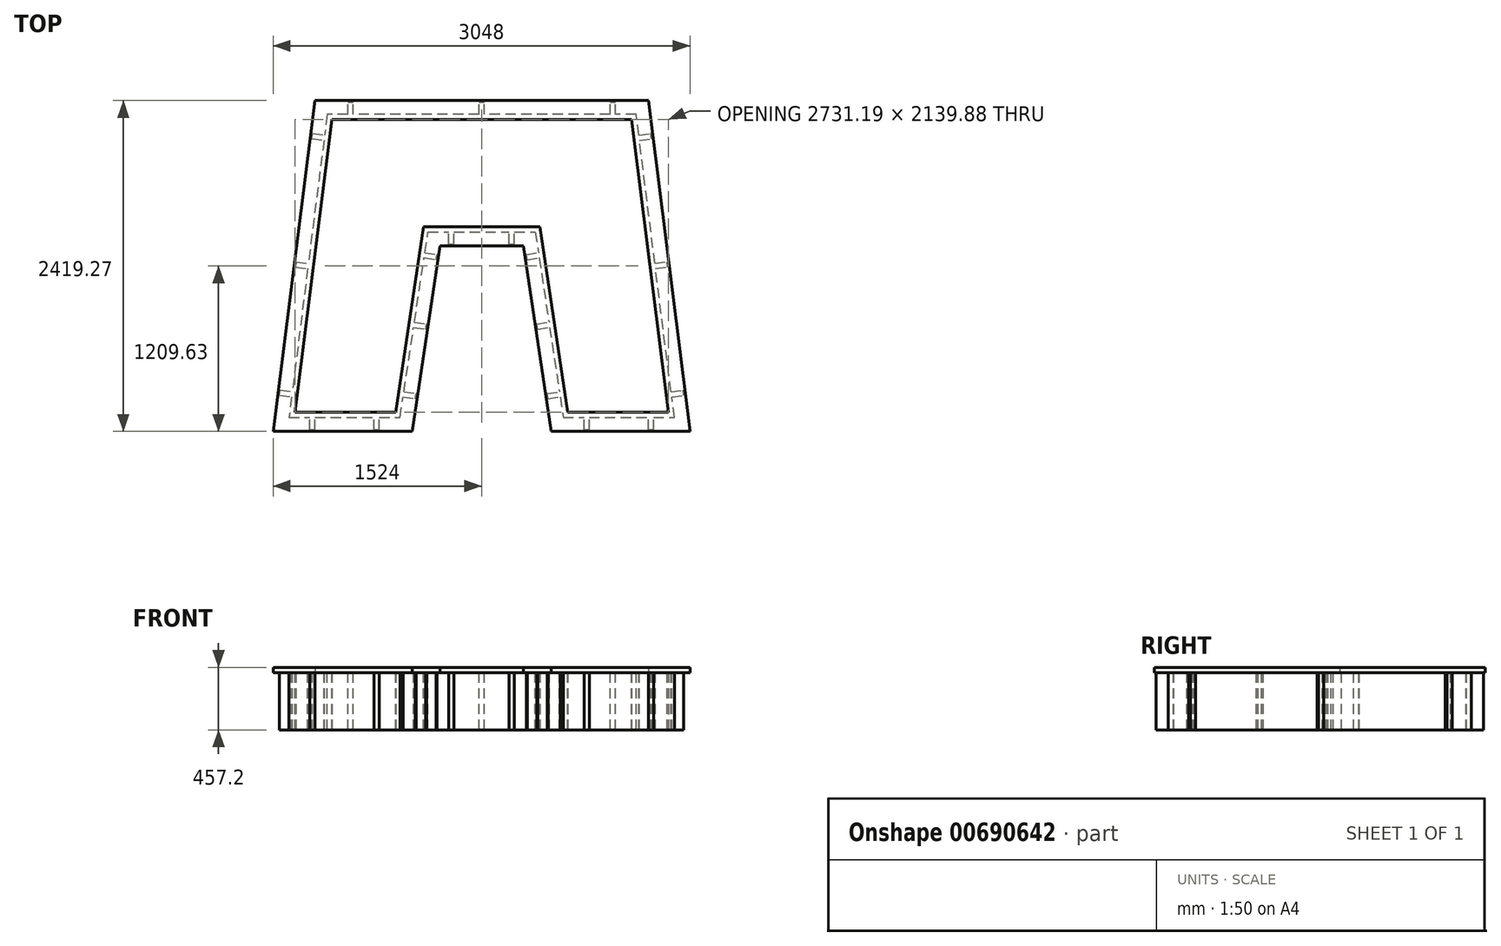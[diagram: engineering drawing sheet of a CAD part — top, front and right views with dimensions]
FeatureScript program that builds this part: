
annotation { "Feature Type Name" : "Feature", "Feature Type Description" : "" }
export const myFeature = defineFeature(function(context is Context, id is Id, definition is map)
    precondition{}
    {
        {
            var Q0;
            Q0=qCreatedBy(makeId("Top.planeOp"),FACE);
            var sketch = newSketch(context, id + "F0", { "sketchPlane" : qUnion([Q0])});
            skLineSegment(sketch, "E0", {"start": v(-1219.2, 0) * mm, "end": v(1219.2, 0) * mm});
            skLineSegment(sketch, "E1", {"start": v(1219.2, 0) * mm, "end": v(1524, -2419.27) * mm});
            skLineSegment(sketch, "E2", {"start": v(1524, -2419.27) * mm, "end": v(509.02, -2419.27) * mm});
            skLineSegment(sketch, "E3", {"start": v(509.02, -2419.27) * mm, "end": v(304.8, -1062.96) * mm});
            skLineSegment(sketch, "E4", {"start": v(304.8, -1062.96) * mm, "end": v(-304.8, -1062.96) * mm});
            skLineSegment(sketch, "E5", {"start": v(-304.8, -1062.96) * mm, "end": v(-509.02, -2419.27) * mm});
            skLineSegment(sketch, "E6", {"start": v(-509.02, -2419.27) * mm, "end": v(-1524, -2419.27) * mm});
            skLineSegment(sketch, "E7", {"start": v(-1524, -2419.27) * mm, "end": v(-1219.2, 0) * mm});
            skLineSegment(sketch, "E8", {"start": v(0, 98.61) * mm, "end": v(0, -258.13) * mm, "construction": true});
            skSolve(sketch);
        }
        {
            var Q0;
            Q0 = qSketchRegion(id + "F0", true);
            extrude(context, id + "F1", {"entities" : qUnion([Q0]), "depth" : 38.1 * mm, "offsetDistance" : 25.4 * mm});
        }
        {
            var Q0;
            Q0=makeQuery(id+"F1.opExtrude","CAP_FACE",FACE,{"disambiguationData":[OSD([sQuery(id+"F0.wireOp",EDGE,"E0"),sQuery(id+"F0.wireOp",EDGE,"E1"),sQuery(id+"F0.wireOp",EDGE,"E2"),sQuery(id+"F0.wireOp",EDGE,"E3"),sQuery(id+"F0.wireOp",EDGE,"E4"),sQuery(id+"F0.wireOp",EDGE,"E5"),sQuery(id+"F0.wireOp",EDGE,"E6"),sQuery(id+"F0.wireOp",EDGE,"E7")])],"isStart":false});
            var sketch = newSketch(context, id + "F2", { "sketchPlane" : qUnion([Q0])});
            skLineSegment(sketch, "E9", {"start": v(-1096, -139.7) * mm, "end": v(-1365.6, -2279.57) * mm});
            skLineSegment(sketch, "E10", {"start": v(-1365.6, -2279.57) * mm, "end": v(-629.26, -2279.57) * mm});
            skLineSegment(sketch, "E11", {"start": v(-629.26, -2279.57) * mm, "end": v(-425.04, -923.26) * mm});
            skLineSegment(sketch, "E12", {"start": v(-425.04, -923.26) * mm, "end": v(425.04, -923.26) * mm});
            skLineSegment(sketch, "E13", {"start": v(425.04, -923.26) * mm, "end": v(629.26, -2279.57) * mm});
            skLineSegment(sketch, "E14", {"start": v(629.26, -2279.57) * mm, "end": v(1365.6, -2279.57) * mm});
            skLineSegment(sketch, "E15", {"start": v(1365.6, -2279.57) * mm, "end": v(1096, -139.7) * mm});
            skLineSegment(sketch, "E16", {"start": v(1096, -139.7) * mm, "end": v(-1096, -139.7) * mm});
            skSolve(sketch);
        }
        {
            var Q0;
            Q0 = qSketchRegion(id + "F2", true);
            extrude(context, id + "F3", {"entities" : qUnion([Q0]), "operationType" : NewBodyOperationType.REMOVE, "endBound" : BoundingType.THROUGH_ALL, "oppositeDirection" : true, "depth" : 30.48 * mm, "offsetDistance" : 30.48 * mm});
        }
        {
            var Q0;
            Q0=makeQuery(id+"F0.imprint","IMPRINT",FACE,{"disambiguationData":[TD([[makeQuery(id+"F0.imprint","IMPRINT",EDGE,{"derivedFrom":sQuery(id+"F0.wireOp",EDGE,"E0")}),-1.0]])]});
            var sketch = newSketch(context, id + "F4", { "sketchPlane" : qUnion([Q0])});
            skLineSegment(sketch, "E17", {"start": v(-1408.8, -2317.67) * mm, "end": v(-596.46, -2317.67) * mm});
            skLineSegment(sketch, "E18", {"start": v(-596.46, -2317.67) * mm, "end": v(-392.25, -961.36) * mm});
            skLineSegment(sketch, "E19", {"start": v(-392.25, -961.36) * mm, "end": v(392.25, -961.36) * mm});
            skLineSegment(sketch, "E20", {"start": v(392.25, -961.36) * mm, "end": v(596.46, -2317.67) * mm});
            skLineSegment(sketch, "E21", {"start": v(596.46, -2317.67) * mm, "end": v(1408.8, -2317.67) * mm});
            skLineSegment(sketch, "E22", {"start": v(1408.8, -2317.67) * mm, "end": v(1129.6, -101.6) * mm});
            skLineSegment(sketch, "E23", {"start": v(1129.6, -101.6) * mm, "end": v(-1129.6, -101.6) * mm});
            skLineSegment(sketch, "E24", {"start": v(-1129.6, -101.6) * mm, "end": v(-1408.8, -2317.67) * mm});
            skLineSegment(sketch, "E25.0", {"start": v(-1365.6, -2279.57) * mm, "end": v(-629.26, -2279.57) * mm});
            skLineSegment(sketch, "E26.0", {"start": v(-1096, -139.7) * mm, "end": v(-1365.6, -2279.57) * mm});
            skLineSegment(sketch, "E27.0", {"start": v(-629.26, -2279.57) * mm, "end": v(-425.04, -923.26) * mm});
            skLineSegment(sketch, "E28.0", {"start": v(-425.04, -923.26) * mm, "end": v(425.04, -923.26) * mm});
            skLineSegment(sketch, "E29.0", {"start": v(425.04, -923.26) * mm, "end": v(629.26, -2279.57) * mm});
            skLineSegment(sketch, "E30.0", {"start": v(629.26, -2279.57) * mm, "end": v(1365.6, -2279.57) * mm});
            skLineSegment(sketch, "E31.0", {"start": v(1365.6, -2279.57) * mm, "end": v(1096, -139.7) * mm});
            skLineSegment(sketch, "E32.0", {"start": v(1096, -139.7) * mm, "end": v(-1096, -139.7) * mm});
            skSolve(sketch);
        }
        {
            var Q0;
            Q0 = qSketchRegion(id + "F4", true);
            extrude(context, id + "F5", {"entities" : qUnion([Q0]), "operationType" : NewBodyOperationType.ADD, "oppositeDirection" : true, "depth" : 419.1 * mm, "offsetDistance" : 30.48 * mm});
        }
        {
            var Q0;
            Q0=makeQuery(id+"F0.imprint","IMPRINT",FACE,{"disambiguationData":[TD([[makeQuery(id+"F0.imprint","IMPRINT",EDGE,{"derivedFrom":sQuery(id+"F0.wireOp",EDGE,"E0")}),-1.0]])]});
            var sketch = newSketch(context, id + "F6", { "sketchPlane" : qUnion([Q0])});
            skLineSegment(sketch, "E33.bottom", {"start": v(-1256.4, -2406.57) * mm, "end": v(-1218.3, -2406.57) * mm});
            skLineSegment(sketch, "E33.top", {"start": v(-1256.4, -2317.67) * mm, "end": v(-1218.3, -2317.67) * mm});
            skLineSegment(sketch, "E33.left", {"start": v(-1256.4, -2406.57) * mm, "end": v(-1256.4, -2317.67) * mm});
            skLineSegment(sketch, "E33.right", {"start": v(-1218.3, -2406.57) * mm, "end": v(-1218.3, -2317.67) * mm});
            skLineSegment(sketch, "E34.bottom", {"start": v(-786.96, -2406.57) * mm, "end": v(-748.86, -2406.57) * mm});
            skLineSegment(sketch, "E34.top", {"start": v(-786.96, -2317.67) * mm, "end": v(-748.86, -2317.67) * mm});
            skLineSegment(sketch, "E34.left", {"start": v(-786.96, -2406.57) * mm, "end": v(-786.96, -2317.67) * mm});
            skLineSegment(sketch, "E34.right", {"start": v(-748.86, -2406.57) * mm, "end": v(-748.86, -2317.67) * mm});
            skLineSegment(sketch, "E35.bottom", {"start": v(748.86, -2406.57) * mm, "end": v(786.96, -2406.57) * mm});
            skLineSegment(sketch, "E35.top", {"start": v(748.86, -2317.67) * mm, "end": v(786.96, -2317.67) * mm});
            skLineSegment(sketch, "E35.left", {"start": v(748.86, -2406.57) * mm, "end": v(748.86, -2317.67) * mm});
            skLineSegment(sketch, "E35.right", {"start": v(786.96, -2406.57) * mm, "end": v(786.96, -2317.67) * mm});
            skLineSegment(sketch, "E36.bottom", {"start": v(1218.3, -2406.57) * mm, "end": v(1256.4, -2406.57) * mm});
            skLineSegment(sketch, "E36.top", {"start": v(1218.3, -2317.67) * mm, "end": v(1256.4, -2317.67) * mm});
            skLineSegment(sketch, "E36.left", {"start": v(1218.3, -2406.57) * mm, "end": v(1218.3, -2317.67) * mm});
            skLineSegment(sketch, "E36.right", {"start": v(1256.4, -2406.57) * mm, "end": v(1256.4, -2317.67) * mm});
            skLineSegment(sketch, "E37.bottom", {"start": v(-573.77, -2166.97) * mm, "end": v(-485.86, -2180.2) * mm});
            skLineSegment(sketch, "E37.top", {"start": v(-568.1, -2129.3) * mm, "end": v(-480.2, -2142.53) * mm});
            skLineSegment(sketch, "E37.left", {"start": v(-573.77, -2166.97) * mm, "end": v(-568.1, -2129.3) * mm});
            skLineSegment(sketch, "E37.right", {"start": v(-485.86, -2180.2) * mm, "end": v(-480.2, -2142.53) * mm});
            skLineSegment(sketch, "E38.bottom", {"start": v(-420.61, -1149.74) * mm, "end": v(-332.7, -1162.98) * mm});
            skLineSegment(sketch, "E38.top", {"start": v(-414.94, -1112.06) * mm, "end": v(-327.03, -1125.3) * mm});
            skLineSegment(sketch, "E38.left", {"start": v(-420.61, -1149.74) * mm, "end": v(-414.94, -1112.06) * mm});
            skLineSegment(sketch, "E38.right", {"start": v(-332.7, -1162.98) * mm, "end": v(-327.03, -1125.3) * mm});
            skLineSegment(sketch, "E39.bottom", {"start": v(-239.85, -1050.26) * mm, "end": v(-201.75, -1050.26) * mm});
            skLineSegment(sketch, "E39.top", {"start": v(-239.85, -961.36) * mm, "end": v(-201.75, -961.36) * mm});
            skLineSegment(sketch, "E39.left", {"start": v(-239.85, -1050.26) * mm, "end": v(-239.85, -961.36) * mm});
            skLineSegment(sketch, "E39.right", {"start": v(-201.75, -1050.26) * mm, "end": v(-201.75, -961.36) * mm});
            skLineSegment(sketch, "E40.bottom", {"start": v(201.75, -1050.26) * mm, "end": v(239.85, -1050.26) * mm});
            skLineSegment(sketch, "E40.top", {"start": v(201.75, -961.36) * mm, "end": v(239.85, -961.36) * mm});
            skLineSegment(sketch, "E40.left", {"start": v(201.75, -1050.26) * mm, "end": v(201.75, -961.36) * mm});
            skLineSegment(sketch, "E40.right", {"start": v(239.85, -1050.26) * mm, "end": v(239.85, -961.36) * mm});
            skLineSegment(sketch, "E41.bottom", {"start": v(485.86, -2180.2) * mm, "end": v(573.77, -2166.97) * mm});
            skLineSegment(sketch, "E41.top", {"start": v(480.2, -2142.53) * mm, "end": v(568.1, -2129.3) * mm});
            skLineSegment(sketch, "E41.left", {"start": v(485.86, -2180.2) * mm, "end": v(480.2, -2142.53) * mm});
            skLineSegment(sketch, "E41.right", {"start": v(573.77, -2166.97) * mm, "end": v(568.1, -2129.3) * mm});
            skLineSegment(sketch, "E42.bottom", {"start": v(332.7, -1162.98) * mm, "end": v(420.61, -1149.74) * mm});
            skLineSegment(sketch, "E42.top", {"start": v(327.03, -1125.3) * mm, "end": v(414.94, -1112.06) * mm});
            skLineSegment(sketch, "E42.left", {"start": v(332.7, -1162.98) * mm, "end": v(327.03, -1125.3) * mm});
            skLineSegment(sketch, "E42.right", {"start": v(420.61, -1149.74) * mm, "end": v(414.94, -1112.06) * mm});
            skLineSegment(sketch, "E43.bottom", {"start": v(-1477.95, -2155.36) * mm, "end": v(-1389.75, -2166.47) * mm});
            skLineSegment(sketch, "E43.top", {"start": v(-1473.19, -2117.56) * mm, "end": v(-1384.98, -2128.67) * mm});
            skLineSegment(sketch, "E43.left", {"start": v(-1477.95, -2155.36) * mm, "end": v(-1473.19, -2117.56) * mm});
            skLineSegment(sketch, "E43.right", {"start": v(-1389.75, -2166.47) * mm, "end": v(-1384.98, -2128.67) * mm});
            skLineSegment(sketch, "E44.bottom", {"start": v(-1241.61, -279.5) * mm, "end": v(-1153.4, -290.6) * mm});
            skLineSegment(sketch, "E44.top", {"start": v(-1236.85, -241.7) * mm, "end": v(-1148.65, -252.8) * mm});
            skLineSegment(sketch, "E44.left", {"start": v(-1241.61, -279.5) * mm, "end": v(-1236.85, -241.7) * mm});
            skLineSegment(sketch, "E44.right", {"start": v(-1153.4, -290.6) * mm, "end": v(-1148.65, -252.8) * mm});
            skLineSegment(sketch, "E45.bottom", {"start": v(-977.2, -101.6) * mm, "end": v(-939.1, -101.6) * mm});
            skLineSegment(sketch, "E45.top", {"start": v(-977.2, -12.7) * mm, "end": v(-939.1, -12.7) * mm});
            skLineSegment(sketch, "E45.left", {"start": v(-977.2, -101.6) * mm, "end": v(-977.2, -12.7) * mm});
            skLineSegment(sketch, "E45.right", {"start": v(-939.1, -101.6) * mm, "end": v(-939.1, -12.7) * mm});
            skLineSegment(sketch, "E46.bottom", {"start": v(939.1, -101.6) * mm, "end": v(977.2, -101.6) * mm});
            skLineSegment(sketch, "E46.top", {"start": v(939.1, -12.7) * mm, "end": v(977.2, -12.7) * mm});
            skLineSegment(sketch, "E46.left", {"start": v(939.1, -101.6) * mm, "end": v(939.1, -12.7) * mm});
            skLineSegment(sketch, "E46.right", {"start": v(977.2, -101.6) * mm, "end": v(977.2, -12.7) * mm});
            skLineSegment(sketch, "E47.bottom", {"start": v(1153.4, -290.6) * mm, "end": v(1241.61, -279.5) * mm});
            skLineSegment(sketch, "E47.top", {"start": v(1148.65, -252.8) * mm, "end": v(1236.85, -241.7) * mm});
            skLineSegment(sketch, "E47.left", {"start": v(1153.4, -290.6) * mm, "end": v(1148.65, -252.8) * mm});
            skLineSegment(sketch, "E47.right", {"start": v(1241.61, -279.5) * mm, "end": v(1236.85, -241.7) * mm});
            skLineSegment(sketch, "E48.bottom", {"start": v(1389.75, -2166.47) * mm, "end": v(1477.95, -2155.36) * mm});
            skLineSegment(sketch, "E48.top", {"start": v(1384.98, -2128.67) * mm, "end": v(1473.19, -2117.56) * mm});
            skLineSegment(sketch, "E48.left", {"start": v(1389.75, -2166.47) * mm, "end": v(1384.98, -2128.67) * mm});
            skLineSegment(sketch, "E48.right", {"start": v(1477.95, -2155.36) * mm, "end": v(1473.19, -2117.56) * mm});
            skLineSegment(sketch, "E49.bottom", {"start": v(-497.2, -1658.36) * mm, "end": v(-409.28, -1671.6) * mm});
            skLineSegment(sketch, "E49.top", {"start": v(-491.52, -1620.68) * mm, "end": v(-403.61, -1633.92) * mm});
            skLineSegment(sketch, "E49.left", {"start": v(-497.2, -1658.36) * mm, "end": v(-491.52, -1620.68) * mm});
            skLineSegment(sketch, "E49.right", {"start": v(-409.28, -1671.6) * mm, "end": v(-403.61, -1633.92) * mm});
            skLineSegment(sketch, "E50.bottom", {"start": v(409.28, -1671.6) * mm, "end": v(497.2, -1658.36) * mm});
            skLineSegment(sketch, "E50.top", {"start": v(403.61, -1633.92) * mm, "end": v(491.52, -1620.68) * mm});
            skLineSegment(sketch, "E50.left", {"start": v(409.28, -1671.6) * mm, "end": v(403.61, -1633.92) * mm});
            skLineSegment(sketch, "E50.right", {"start": v(497.2, -1658.36) * mm, "end": v(491.52, -1620.68) * mm});
            skLineSegment(sketch, "E51.bottom", {"start": v(1271.58, -1228.54) * mm, "end": v(1359.78, -1217.43) * mm});
            skLineSegment(sketch, "E51.top", {"start": v(1266.82, -1190.74) * mm, "end": v(1355.02, -1179.62) * mm});
            skLineSegment(sketch, "E51.left", {"start": v(1271.58, -1228.54) * mm, "end": v(1266.82, -1190.74) * mm});
            skLineSegment(sketch, "E51.right", {"start": v(1359.78, -1217.43) * mm, "end": v(1355.02, -1179.62) * mm});
            skLineSegment(sketch, "E52.bottom", {"start": v(-1359.78, -1217.43) * mm, "end": v(-1271.58, -1228.54) * mm});
            skLineSegment(sketch, "E52.top", {"start": v(-1355.02, -1179.62) * mm, "end": v(-1266.82, -1190.74) * mm});
            skLineSegment(sketch, "E52.left", {"start": v(-1359.78, -1217.43) * mm, "end": v(-1355.02, -1179.62) * mm});
            skLineSegment(sketch, "E52.right", {"start": v(-1271.58, -1228.54) * mm, "end": v(-1266.82, -1190.74) * mm});
            skLineSegment(sketch, "E53.bottom", {"start": v(-19.05, -101.6) * mm, "end": v(19.05, -101.6) * mm});
            skLineSegment(sketch, "E53.top", {"start": v(-19.05, -12.7) * mm, "end": v(19.05, -12.7) * mm});
            skLineSegment(sketch, "E53.left", {"start": v(-19.05, -101.6) * mm, "end": v(-19.05, -12.7) * mm});
            skLineSegment(sketch, "E53.right", {"start": v(19.05, -101.6) * mm, "end": v(19.05, -12.7) * mm});
            skSolve(sketch);
        }
        {
            var Q0;
            Q0 = qSketchRegion(id + "F6", true);
            var Q1;
            Q1=makeQuery(id+"F5.opExtrude","CAP_FACE",FACE,{"disambiguationData":[OSD([sQuery(id+"F4.wireOp",EDGE,"E17"),sQuery(id+"F4.wireOp",EDGE,"E18"),sQuery(id+"F4.wireOp",EDGE,"E19"),sQuery(id+"F4.wireOp",EDGE,"E20"),sQuery(id+"F4.wireOp",EDGE,"E21"),sQuery(id+"F4.wireOp",EDGE,"E22"),sQuery(id+"F4.wireOp",EDGE,"E23"),sQuery(id+"F4.wireOp",EDGE,"E24"),sQuery(id+"F4.wireOp",EDGE,"E25.0"),sQuery(id+"F4.wireOp",EDGE,"E26.0"),sQuery(id+"F4.wireOp",EDGE,"E27.0"),sQuery(id+"F4.wireOp",EDGE,"E28.0"),sQuery(id+"F4.wireOp",EDGE,"E29.0"),sQuery(id+"F4.wireOp",EDGE,"E30.0"),sQuery(id+"F4.wireOp",EDGE,"E31.0"),sQuery(id+"F4.wireOp",EDGE,"E32.0")])],"isStart":false});
            extrude(context, id + "F7", {"entities" : qUnion([Q0]), "operationType" : NewBodyOperationType.ADD, "endBound" : BoundingType.UP_TO_SURFACE, "oppositeDirection" : true, "depth" : 30.48 * mm, "endBoundEntityFace" : qUnion([Q1]), "offsetDistance" : 30.48 * mm});
        }
        {
            var Q0;
            {var subQ0=sQuery(id+"F4.wireOp",EDGE,"E32.0");var subQ1=sQuery(id+"F4.wireOp",EDGE,"E31.0");var subQ2=sQuery(id+"F4.wireOp",EDGE,"E30.0");var subQ3=sQuery(id+"F4.wireOp",EDGE,"E29.0");var subQ4=sQuery(id+"F4.wireOp",EDGE,"E28.0");var subQ5=sQuery(id+"F4.wireOp",EDGE,"E27.0");var subQ6=sQuery(id+"F4.wireOp",EDGE,"E26.0");var subQ7=sQuery(id+"F4.wireOp",EDGE,"E25.0");var subQ8=sQuery(id+"F4.wireOp",EDGE,"E24");var subQ9=sQuery(id+"F4.wireOp",EDGE,"E23");var subQ10=sQuery(id+"F4.wireOp",EDGE,"E22");var subQ11=sQuery(id+"F4.wireOp",EDGE,"E21");var subQ12=sQuery(id+"F4.wireOp",EDGE,"E20");var subQ13=sQuery(id+"F4.wireOp",EDGE,"E19");var subQ14=sQuery(id+"F4.wireOp",EDGE,"E18");var subQ15=sQuery(id+"F4.wireOp",EDGE,"E17");Q0=makeQuery(id+"F7.boolean.opBoolean","MERGE",FACE,{"derivedFrom":[makeQuery(id+"F5.opExtrude","CAP_FACE",FACE,{"disambiguationData":[OSD([subQ15,subQ14,subQ13,subQ12,subQ11,subQ10,subQ9,subQ8,subQ7,subQ6,subQ5,subQ4,subQ3,subQ2,subQ1,subQ0])],"isStart":false}),makeQuery(id+"F7.opExtrude","CAP_FACE",FACE,{"disambiguationData":[OSD([subQ15,subQ14,subQ13,subQ12,subQ11,subQ10,subQ9,subQ8,subQ7,subQ6,subQ5,subQ4,subQ3,subQ2,subQ1,subQ0]),OD(0.0)],"isStart":false}),makeQuery(id+"F7.opExtrude","CAP_FACE",FACE,{"disambiguationData":[OSD([subQ15,subQ14,subQ13,subQ12,subQ11,subQ10,subQ9,subQ8,subQ7,subQ6,subQ5,subQ4,subQ3,subQ2,subQ1,subQ0]),OD(1.0)],"isStart":false}),makeQuery(id+"F7.opExtrude","CAP_FACE",FACE,{"disambiguationData":[OSD([subQ15,subQ14,subQ13,subQ12,subQ11,subQ10,subQ9,subQ8,subQ7,subQ6,subQ5,subQ4,subQ3,subQ2,subQ1,subQ0]),OD(2.0)],"isStart":false}),makeQuery(id+"F7.opExtrude","CAP_FACE",FACE,{"disambiguationData":[OSD([subQ15,subQ14,subQ13,subQ12,subQ11,subQ10,subQ9,subQ8,subQ7,subQ6,subQ5,subQ4,subQ3,subQ2,subQ1,subQ0]),OD(3.0)],"isStart":false}),makeQuery(id+"F7.opExtrude","CAP_FACE",FACE,{"disambiguationData":[OSD([subQ15,subQ14,subQ13,subQ12,subQ11,subQ10,subQ9,subQ8,subQ7,subQ6,subQ5,subQ4,subQ3,subQ2,subQ1,subQ0]),OD(4.0)],"isStart":false}),makeQuery(id+"F7.opExtrude","CAP_FACE",FACE,{"disambiguationData":[OSD([subQ15,subQ14,subQ13,subQ12,subQ11,subQ10,subQ9,subQ8,subQ7,subQ6,subQ5,subQ4,subQ3,subQ2,subQ1,subQ0]),OD(5.0)],"isStart":false}),makeQuery(id+"F7.opExtrude","CAP_FACE",FACE,{"disambiguationData":[OSD([subQ15,subQ14,subQ13,subQ12,subQ11,subQ10,subQ9,subQ8,subQ7,subQ6,subQ5,subQ4,subQ3,subQ2,subQ1,subQ0]),OD(6.0)],"isStart":false}),makeQuery(id+"F7.opExtrude","CAP_FACE",FACE,{"disambiguationData":[OSD([subQ15,subQ14,subQ13,subQ12,subQ11,subQ10,subQ9,subQ8,subQ7,subQ6,subQ5,subQ4,subQ3,subQ2,subQ1,subQ0]),OD(7.0)],"isStart":false}),makeQuery(id+"F7.opExtrude","CAP_FACE",FACE,{"disambiguationData":[OSD([subQ15,subQ14,subQ13,subQ12,subQ11,subQ10,subQ9,subQ8,subQ7,subQ6,subQ5,subQ4,subQ3,subQ2,subQ1,subQ0]),OD(8.0)],"isStart":false}),makeQuery(id+"F7.opExtrude","CAP_FACE",FACE,{"disambiguationData":[OSD([subQ15,subQ14,subQ13,subQ12,subQ11,subQ10,subQ9,subQ8,subQ7,subQ6,subQ5,subQ4,subQ3,subQ2,subQ1,subQ0]),OD(9.0)],"isStart":false}),makeQuery(id+"F7.opExtrude","CAP_FACE",FACE,{"disambiguationData":[OSD([subQ15,subQ14,subQ13,subQ12,subQ11,subQ10,subQ9,subQ8,subQ7,subQ6,subQ5,subQ4,subQ3,subQ2,subQ1,subQ0]),OD(10.0)],"isStart":false}),makeQuery(id+"F7.opExtrude","CAP_FACE",FACE,{"disambiguationData":[OSD([subQ15,subQ14,subQ13,subQ12,subQ11,subQ10,subQ9,subQ8,subQ7,subQ6,subQ5,subQ4,subQ3,subQ2,subQ1,subQ0]),OD(11.0)],"isStart":false}),makeQuery(id+"F7.opExtrude","CAP_FACE",FACE,{"disambiguationData":[OSD([subQ15,subQ14,subQ13,subQ12,subQ11,subQ10,subQ9,subQ8,subQ7,subQ6,subQ5,subQ4,subQ3,subQ2,subQ1,subQ0]),OD(12.0)],"isStart":false}),makeQuery(id+"F7.opExtrude","CAP_FACE",FACE,{"disambiguationData":[OSD([subQ15,subQ14,subQ13,subQ12,subQ11,subQ10,subQ9,subQ8,subQ7,subQ6,subQ5,subQ4,subQ3,subQ2,subQ1,subQ0]),OD(13.0)],"isStart":false}),makeQuery(id+"F7.opExtrude","CAP_FACE",FACE,{"disambiguationData":[OSD([subQ15,subQ14,subQ13,subQ12,subQ11,subQ10,subQ9,subQ8,subQ7,subQ6,subQ5,subQ4,subQ3,subQ2,subQ1,subQ0]),OD(14.0)],"isStart":false}),makeQuery(id+"F7.opExtrude","CAP_FACE",FACE,{"disambiguationData":[OSD([subQ15,subQ14,subQ13,subQ12,subQ11,subQ10,subQ9,subQ8,subQ7,subQ6,subQ5,subQ4,subQ3,subQ2,subQ1,subQ0]),OD(15.0)],"isStart":false}),makeQuery(id+"F7.opExtrude","CAP_FACE",FACE,{"disambiguationData":[OSD([subQ15,subQ14,subQ13,subQ12,subQ11,subQ10,subQ9,subQ8,subQ7,subQ6,subQ5,subQ4,subQ3,subQ2,subQ1,subQ0]),OD(16.0)],"isStart":false}),makeQuery(id+"F7.opExtrude","CAP_FACE",FACE,{"disambiguationData":[OSD([subQ15,subQ14,subQ13,subQ12,subQ11,subQ10,subQ9,subQ8,subQ7,subQ6,subQ5,subQ4,subQ3,subQ2,subQ1,subQ0]),OD(17.0)],"isStart":false}),makeQuery(id+"F7.opExtrude","CAP_FACE",FACE,{"disambiguationData":[OSD([subQ15,subQ14,subQ13,subQ12,subQ11,subQ10,subQ9,subQ8,subQ7,subQ6,subQ5,subQ4,subQ3,subQ2,subQ1,subQ0]),OD(18.0)],"isStart":false}),makeQuery(id+"F7.opExtrude","CAP_FACE",FACE,{"disambiguationData":[OSD([subQ15,subQ14,subQ13,subQ12,subQ11,subQ10,subQ9,subQ8,subQ7,subQ6,subQ5,subQ4,subQ3,subQ2,subQ1,subQ0]),OD(19.0)],"isStart":false}),makeQuery(id+"F7.opExtrude","CAP_FACE",FACE,{"disambiguationData":[OSD([subQ15,subQ14,subQ13,subQ12,subQ11,subQ10,subQ9,subQ8,subQ7,subQ6,subQ5,subQ4,subQ3,subQ2,subQ1,subQ0]),OD(20.0)],"isStart":false})]});}
            var sketch = newSketch(context, id + "F8", { "sketchPlane" : qUnion([Q0])});
            skLineSegment(sketch, "E54.0", {"start": v(-1365.6, 2279.57) * mm, "end": v(-629.26, 2279.57) * mm});
            skLineSegment(sketch, "E55.0", {"start": v(-629.26, 2279.57) * mm, "end": v(-425.04, 923.26) * mm});
            skLineSegment(sketch, "E56.0", {"start": v(-425.04, 923.26) * mm, "end": v(425.04, 923.26) * mm});
            skLineSegment(sketch, "E57.0", {"start": v(425.04, 923.26) * mm, "end": v(629.26, 2279.57) * mm});
            skLineSegment(sketch, "E58.0", {"start": v(629.26, 2279.57) * mm, "end": v(1365.6, 2279.57) * mm});
            skLineSegment(sketch, "E59.0", {"start": v(1365.6, 2279.57) * mm, "end": v(1096, 139.7) * mm});
            skLineSegment(sketch, "E60.0", {"start": v(1096, 139.7) * mm, "end": v(-1096, 139.7) * mm});
            skLineSegment(sketch, "E61.0", {"start": v(-1096, 139.7) * mm, "end": v(-1365.6, 2279.57) * mm});
            skSolve(sketch);
        }
        {
            var Q0;
            Q0 = qSketchRegion(id + "F8", true);
            var Q1;
            Q1=makeQuery(id+"F1.opExtrude","CAP_FACE",FACE,{"disambiguationData":[OSD([sQuery(id+"F0.wireOp",EDGE,"E0"),sQuery(id+"F0.wireOp",EDGE,"E1"),sQuery(id+"F0.wireOp",EDGE,"E2"),sQuery(id+"F0.wireOp",EDGE,"E3"),sQuery(id+"F0.wireOp",EDGE,"E4"),sQuery(id+"F0.wireOp",EDGE,"E5"),sQuery(id+"F0.wireOp",EDGE,"E6"),sQuery(id+"F0.wireOp",EDGE,"E7")])],"isStart":true});
            extrude(context, id + "F9", {"entities" : qUnion([Q0]), "endBound" : BoundingType.UP_TO_SURFACE, "oppositeDirection" : true, "depth" : 30.48 * mm, "endBoundEntityFace" : qUnion([Q1]), "offsetDistance" : 30.48 * mm});
        }
    });
